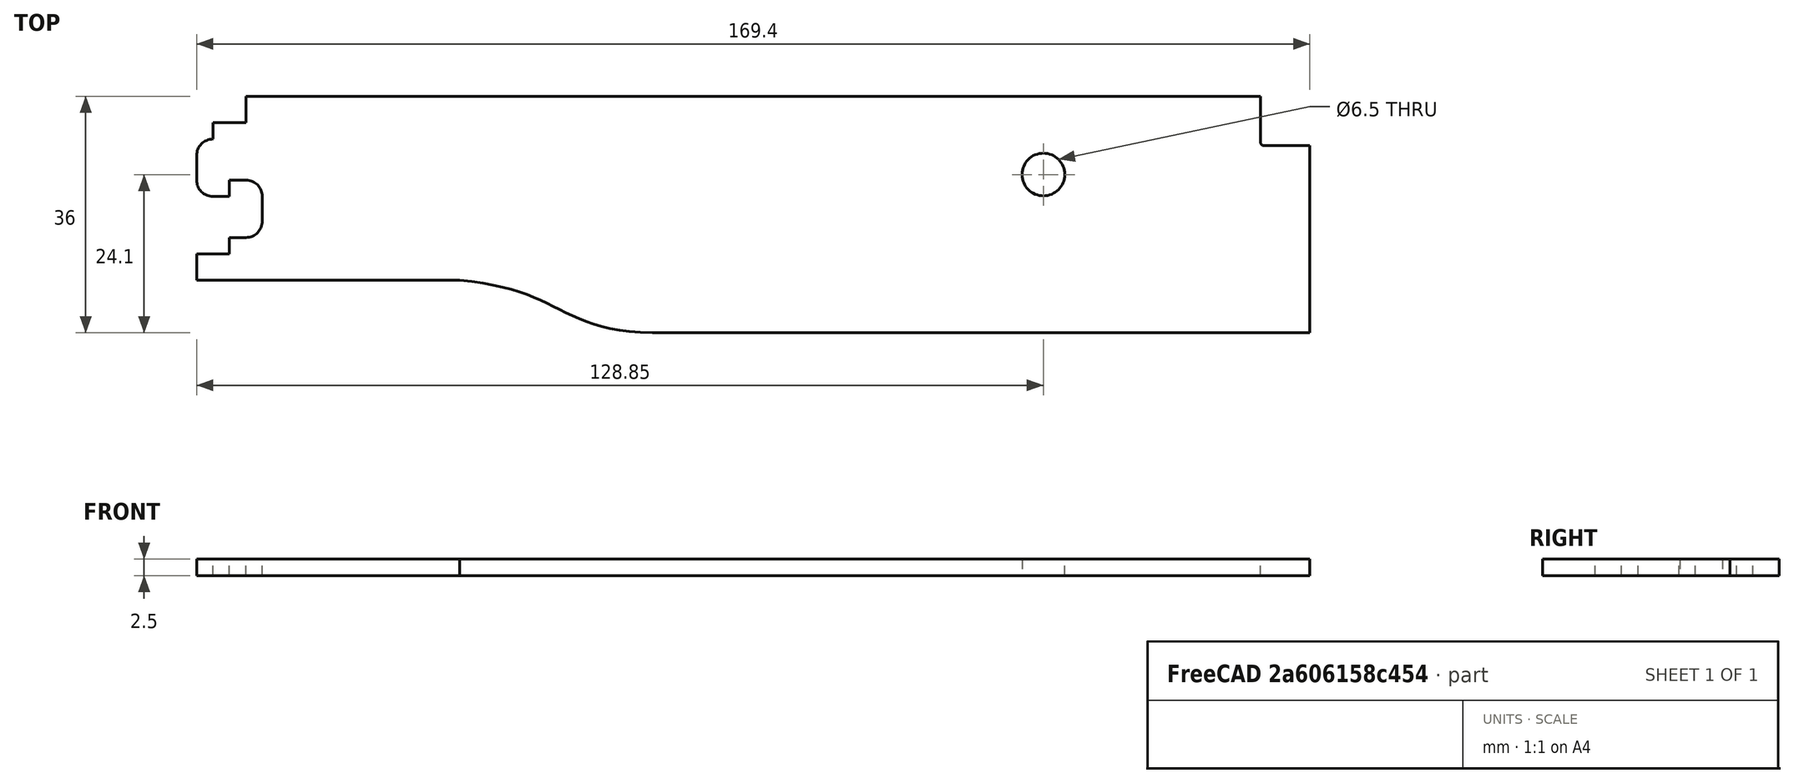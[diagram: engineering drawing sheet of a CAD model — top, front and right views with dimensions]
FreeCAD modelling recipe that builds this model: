
FCSTD DOCUMENT  (FreeCAD 0.19R0.19.2)
Label: v0_11
License: All rights reserved
LicenseURL: http://en.wikipedia.org/wiki/All_rights_reserved
objects: Sketcher::SketchObject×2, Part::Extrusion×1
note: 3 computed .brp shape members not serialized (recipe doc carries the construction recipe); baked Part::Feature solids carry a one-line shape summary decoded from their .brp

FEATURE [Sketcher::SketchObject] Sketch
  FullyConstrained = true
  sketch-geometry (33):
    g0: LineSegment StartX=0 StartY=0 StartZ=0 EndX=154.4 EndY=0 EndZ=0
    g1: LineSegment StartX=154.4 StartY=0 StartZ=0 EndX=154.4 EndY=-7 EndZ=0
    g2: LineSegment StartX=154.9 StartY=-7.5 StartZ=0 EndX=161.9 EndY=-7.5 EndZ=0
    g3: ArcOfCircle CenterX=154.9 CenterY=-7 CenterZ=0 NormalX=0 NormalY=0 NormalZ=1 AngleXU=0 Radius=0.5 StartAngle=3.14159 EndAngle=4.71239
    g4: Circle CenterX=121.35 CenterY=-11.9 CenterZ=0 NormalX=0 NormalY=0 NormalZ=1 AngleXU=0 Radius=3.25
    g5: LineSegment StartX=0 StartY=0 StartZ=0 EndX=0 EndY=-4 EndZ=0
    g6: LineSegment StartX=-5 StartY=-4 StartZ=0 EndX=0 EndY=-4 EndZ=0
    g7: LineSegment StartX=-5 StartY=-4 StartZ=0 EndX=-5 EndY=-6.5 EndZ=0
    g8: LineSegment StartX=-7.5 StartY=-9 StartZ=0 EndX=-7.5 EndY=-12.75 EndZ=0
    g9: ArcOfCircle CenterX=-5 CenterY=-9 CenterZ=0 NormalX=0 NormalY=0 NormalZ=1 AngleXU=0 Radius=2.5 StartAngle=1.5708 EndAngle=3.14159
    g10: LineSegment StartX=-5 StartY=-15.25 StartZ=0 EndX=-2.5 EndY=-15.25 EndZ=0
    g11: ArcOfCircle CenterX=-5 CenterY=-12.75 CenterZ=0 NormalX=0 NormalY=0 NormalZ=1 AngleXU=0 Radius=2.5 StartAngle=3.14159 EndAngle=4.71239
    g12: LineSegment StartX=-2.5 StartY=-15.25 StartZ=0 EndX=-2.5 EndY=-12.75 EndZ=0
    g13: LineSegment StartX=-2.5 StartY=-12.75 StartZ=0 EndX=1.488e-13 EndY=-12.75 EndZ=0
    g14: ArcOfCircle CenterX=1.486e-13 CenterY=-15.25 CenterZ=0 NormalX=0 NormalY=0 NormalZ=1 AngleXU=0 Radius=2.5 StartAngle=8e-16 EndAngle=1.5708
    g15: LineSegment StartX=2.5 StartY=-15.25 StartZ=0 EndX=2.5 EndY=-19 EndZ=0
    g16: ArcOfCircle CenterX=1.483e-13 CenterY=-19 CenterZ=0 NormalX=0 NormalY=0 NormalZ=1 AngleXU=0 Radius=2.5 StartAngle=4.71239 EndAngle=6.28319
    g17: LineSegment StartX=-2.5 StartY=-21.5 StartZ=0 EndX=1.479e-13 EndY=-21.5 EndZ=0
    g18: LineSegment StartX=-2.5 StartY=-21.5 StartZ=0 EndX=-2.5 EndY=-24 EndZ=0
    g19: LineSegment StartX=-7.5 StartY=-24 StartZ=0 EndX=-2.5 EndY=-24 EndZ=0
    g20: LineSegment StartX=-7.5 StartY=-24 StartZ=0 EndX=-7.5 EndY=-28 EndZ=0
    g21: LineSegment StartX=161.9 StartY=-7.5 StartZ=0 EndX=161.9 EndY=-36 EndZ=0
    g22: LineSegment StartX=61.85 StartY=-36 StartZ=0 EndX=161.9 EndY=-36 EndZ=0
    g23-g27: Circle x5 (B-spline internal-alignment scaffolding for g28; pole/knot coordinates omitted)
    g28: BSplineCurve PolesCount=5 KnotsCount=3 Degree=3 IsPeriodic=0
    g29: GeomPoint X=61.85 Y=-36 Z=0
    g30: GeomPoint X=47.2264 Y=-32.2128 Z=0
    g31: GeomPoint X=32.5209 Y=-28 Z=0
    g32: LineSegment StartX=32.5209 StartY=-28 StartZ=0 EndX=-7.5 EndY=-28 EndZ=0
  constraints (75):
    c: PointOnObject(g0,g-2)
    c: Horizontal(g0)
    c: Distance(g0) = 154.4
    c: DistanceY(g-1,g0) = 0
    c: Vertical(g1)
    c: Distance(g1) = 7
    c: Coincident(g1,g0)
    c: Horizontal(g2)
    c: Distance(g2) = 7
    c: Coincident(g3,g1)
    c: Tangent(g2,g3)
    c: Tangent(g2,g3,g2) = -1.5708
    c: Block(g3)
    c: Block(g4)
    c: Vertical(g5)
    c: Distance(g5) = 4
    c: Coincident(g5,g0)
    c: Horizontal(g6)
    c: Distance(g6) = 5
    c: Coincident(g6,g5)
    c: Vertical(g7)
    c: Distance(g7) = 2.5
    c: Coincident(g7,g6)
    c: Vertical(g8)
    c: Distance(g8) = 3.75
    c: Coincident(g9,g7)
    c: Block(g9)
    c: Coincident(g8,g9)
    c: Horizontal(g10)
    c: Distance(g10) = 2.5
    c: Coincident(g11,g8)
    c: Block(g11)
    c: Block(g10)
    c: Vertical(g12)
    c: Distance(g12) = 2.5
    c: Coincident(g12,g10)
    c: Horizontal(g13)
    c: Distance(g13) = 2.5
    c: Coincident(g13,g12)
    c: Coincident(g14,g13)
    c: Vertical(g15)
    c: Distance(g15) = 3.75
    c: Block(g14)
    c: Coincident(g15,g14)
    c: Coincident(g16,g15)
    c: Block(g16)
    c: Horizontal(g17)
    c: Distance(g17) = 2.5
    c: Coincident(g17,g16)
    c: Vertical(g18)
    c: Distance(g18) = 2.5
    c: Coincident(g18,g17)
    c: Horizontal(g19)
    c: Distance(g19) = 5
    c: Coincident(g19,g18)
    c: Vertical(g20)
    c: Distance(g20) = 4
    c: Coincident(g20,g19)
    c: Vertical(g21)
    c: Distance(g21) = 28.5
    c: Coincident(g21,g2)
    c: Horizontal(g22)
    c: Distance(g22) = 100.05
    c: Coincident(g22,g21)
    c: Coincident(g28,g22)
    c: Weight(g23) = 1
    c: Equal(g23, g24-g27) x4
    c: InternalAlignment(g23-g27 -> g28) x5
    c: InternalAlignment(g29,g28)
    c: InternalAlignment(g30,g28)
    c: InternalAlignment(g31,g28)
    c: Horizontal(g32)
    c: Coincident(g32,g20)
    c: Coincident(g32,g28)
    c: Block(g28)
FEATURE [Part::Extrusion] Extrude
  Base = -> Sketch
  Dir = (0,0,1)
  DirMode = 2
  FaceMakerClass = Part::FaceMakerBullseye
  LengthFwd = 2.5
  LengthRev = 0
  Solid = true
  Symmetric = false
FEATURE [Sketcher::SketchObject] Sketch001
  FullyConstrained = true
  sketch-geometry (60):
    g0: LineSegment StartX=0 StartY=0 StartZ=0 EndX=154.4 EndY=0 EndZ=0
    g1: LineSegment StartX=154.9 StartY=-7.5 StartZ=0 EndX=161.9 EndY=-7.5 EndZ=0
    g2: ArcOfCircle CenterX=154.9 CenterY=-7 CenterZ=0 NormalX=0 NormalY=0 NormalZ=1 AngleXU=0 Radius=0.5 StartAngle=3.14159 EndAngle=4.71239
    g3: Circle CenterX=121.35 CenterY=-11.9 CenterZ=0 NormalX=0 NormalY=0 NormalZ=1 AngleXU=0 Radius=3.25
    g4: LineSegment StartX=0 StartY=0 StartZ=0 EndX=0 EndY=-4 EndZ=0
    g5: LineSegment StartX=-5 StartY=-4 StartZ=0 EndX=0 EndY=-4 EndZ=0
    g6: LineSegment StartX=-5 StartY=-4 StartZ=0 EndX=-5 EndY=-6.5 EndZ=0
    g7: LineSegment StartX=-7.50066 StartY=-9 StartZ=0 EndX=-7.50066 EndY=-12.75 EndZ=0
    g8: ArcOfCircle CenterX=-5.00066 CenterY=-9 CenterZ=0 NormalX=0 NormalY=0 NormalZ=1 AngleXU=0 Radius=2.5 StartAngle=1.57053 EndAngle=3.14159
    g9: LineSegment StartX=-5 StartY=-15.25 StartZ=0 EndX=-2.5 EndY=-15.25 EndZ=0
    g10: ArcOfCircle CenterX=-5 CenterY=-12.75 CenterZ=0 NormalX=0 NormalY=0 NormalZ=1 AngleXU=0 Radius=2.50066 StartAngle=3.14159 EndAngle=4.71239
    g11: LineSegment StartX=-2.5 StartY=-15.25 StartZ=0 EndX=-2.5 EndY=-12.75 EndZ=0
    g12: LineSegment StartX=-2.5 StartY=-12.75 StartZ=0 EndX=1.488e-13 EndY=-12.75 EndZ=0
    g13: ArcOfCircle CenterX=1.486e-13 CenterY=-15.25 CenterZ=0 NormalX=0 NormalY=0 NormalZ=1 AngleXU=0 Radius=2.5 StartAngle=8e-16 EndAngle=1.5708
    g14: LineSegment StartX=2.5 StartY=-15.25 StartZ=0 EndX=2.5 EndY=-19 EndZ=0
    g15: ArcOfCircle CenterX=1.483e-13 CenterY=-19 CenterZ=0 NormalX=0 NormalY=0 NormalZ=1 AngleXU=0 Radius=2.5 StartAngle=4.71239 EndAngle=6.28319
    g16: LineSegment StartX=-2.5 StartY=-21.5 StartZ=0 EndX=1.812e-13 EndY=-21.5 EndZ=0
    g17: LineSegment StartX=-2.5 StartY=-21.5 StartZ=0 EndX=-2.5 EndY=-24 EndZ=0
    g18: LineSegment StartX=-7.5 StartY=-24 StartZ=0 EndX=-2.5 EndY=-24 EndZ=0
    g19: LineSegment StartX=-7.5 StartY=-24 StartZ=0 EndX=-7.5 EndY=-28 EndZ=0
    g20: LineSegment StartX=161.9 StartY=-7.5 StartZ=0 EndX=161.9 EndY=-36 EndZ=0
    g21: LineSegment StartX=61.85 StartY=-36 StartZ=0 EndX=161.9 EndY=-36 EndZ=0
    g22-g26: Circle x5 (B-spline internal-alignment scaffolding for g27; pole/knot coordinates omitted)
    g27: BSplineCurve PolesCount=5 KnotsCount=3 Degree=3 IsPeriodic=0
    g28: GeomPoint X=61.85 Y=-36 Z=0
    g29: GeomPoint X=47.2264 Y=-32.2128 Z=0
    g30: GeomPoint X=32.5209 Y=-28 Z=0
    g31: LineSegment StartX=154.4 StartY=0 StartZ=0 EndX=154.4 EndY=-3 EndZ=0
    g32: ArcOfCircle CenterX=154.9 CenterY=-7 CenterZ=0 NormalX=0 NormalY=0 NormalZ=1 AngleXU=0 Radius=3.5 StartAngle=3.14159 EndAngle=4.71239
    g33: LineSegment StartX=161.9 StartY=-7.5 StartZ=0 EndX=161.9 EndY=-10.5 EndZ=0
    g34: Circle CenterX=121.35 CenterY=-11.9 CenterZ=0 NormalX=0 NormalY=0 NormalZ=1 AngleXU=0 Radius=6.25
    g35: LineSegment StartX=154.9 StartY=-10.5 StartZ=0 EndX=158.4 EndY=-10.5 EndZ=0
    g36: ArcOfCircle CenterX=158.4 CenterY=-11 CenterZ=0 NormalX=0 NormalY=0 NormalZ=1 AngleXU=0 Radius=0.5 StartAngle=0 EndAngle=1.5708
    g37: LineSegment StartX=161.9 StartY=-36 StartZ=0 EndX=158.9 EndY=-36 EndZ=0
    g38: ArcOfCircle CenterX=158.4 CenterY=-32.5 CenterZ=0 NormalX=0 NormalY=0 NormalZ=1 AngleXU=0 Radius=0.5 StartAngle=4.71239 EndAngle=6.28319
    g39: LineSegment StartX=158.9 StartY=-11 StartZ=0 EndX=158.9 EndY=-32.5 EndZ=0
    g40: LineSegment StartX=61.85 StartY=-33 StartZ=0 EndX=158.4 EndY=-33 EndZ=0
    g41: LineSegment StartX=151.4 StartY=-7 StartZ=0 EndX=151.4 EndY=-3.5 EndZ=0
    g42: ArcOfCircle CenterX=150.9 CenterY=-3.5 CenterZ=0 NormalX=0 NormalY=0 NormalZ=1 AngleXU=0 Radius=0.5 StartAngle=-5.0484e-12 EndAngle=1.5708
    g43: LineSegment StartX=0 StartY=0 StartZ=0 EndX=5 EndY=0 EndZ=0
    g44: ArcOfCircle CenterX=8 CenterY=-6 CenterZ=0 NormalX=0 NormalY=0 NormalZ=1 AngleXU=0 Radius=3 StartAngle=1.5708 EndAngle=3.14159
    g45: LineSegment StartX=8 StartY=-3 StartZ=0 EndX=150.9 EndY=-3 EndZ=0
    g46: LineSegment StartX=154.4 StartY=-3 StartZ=0 EndX=154.4 EndY=-7 EndZ=0
    g47: LineSegment StartX=5 StartY=-6 StartZ=0 EndX=5 EndY=-22 EndZ=0
    g48: LineSegment StartX=-7.5 StartY=-28 StartZ=0 EndX=32.5209 EndY=-28 EndZ=0
    g49: ArcOfCircle CenterX=8 CenterY=-22 CenterZ=0 NormalX=0 NormalY=0 NormalZ=1 AngleXU=0 Radius=3 StartAngle=3.14159 EndAngle=4.71239
    g50: LineSegment StartX=8 StartY=-25 StartZ=0 EndX=32.52 EndY=-25 EndZ=0
    g51-g55: Circle x5 (B-spline internal-alignment scaffolding for g56; pole/knot coordinates omitted)
    g56: BSplineCurve PolesCount=5 KnotsCount=3 Degree=3 IsPeriodic=0
    g57: GeomPoint X=32.52 Y=-25 Z=0
    g58: GeomPoint X=47.2188 Y=-29.105 Z=0
    g59: GeomPoint X=61.85 Y=-33 Z=0
  constraints (127):
    c: PointOnObject(g0,g-2)
    c: Horizontal(g0)
    c: Distance(g0) = 154.4
    c: DistanceY(g-1,g0) = 0
    c: Horizontal(g1)
    c: Distance(g1) = 7
    c: Tangent(g1,g2)
    c: Tangent(g1,g2,g1) = -1.5708
    c: Block(g2)
    c: Block(g3)
    c: Vertical(g4)
    c: Distance(g4) = 4
    c: Coincident(g4,g0)
    c: Horizontal(g5)
    c: Distance(g5) = 5
    c: Coincident(g5,g4)
    c: Vertical(g6)
    c: Distance(g6) = 2.5
    c: Coincident(g6,g5)
    c: Vertical(g7)
    c: Distance(g7) = 3.75
    c: Coincident(g8,g6)
    c: Block(g8)
    c: Coincident(g7,g8)
    c: Horizontal(g9)
    c: Distance(g9) = 2.5
    c: Coincident(g10,g7)
    c: Block(g10)
    c: Block(g9)
    c: Vertical(g11)
    c: Distance(g11) = 2.5
    c: Coincident(g11,g9)
    c: Horizontal(g12)
    c: Distance(g12) = 2.5
    c: Coincident(g12,g11)
    c: Coincident(g13,g12)
    c: Vertical(g14)
    c: Distance(g14) = 3.75
    c: Block(g13)
    c: Coincident(g14,g13)
    c: Coincident(g15,g14)
    c: Block(g15)
    c: Horizontal(g16)
    c: Distance(g16) = 2.5
    c: Coincident(g16,g15)
    c: Vertical(g17)
    c: Distance(g17) = 2.5
    c: Coincident(g17,g16)
    c: Horizontal(g18)
    c: Distance(g18) = 5
    c: Coincident(g18,g17)
    c: Vertical(g19)
    c: Distance(g19) = 4
    c: Coincident(g19,g18)
    c: Vertical(g20)
    c: Distance(g20) = 28.5
    c: Coincident(g20,g1)
    c: Horizontal(g21)
    c: Distance(g21) = 100.05
    c: Coincident(g21,g20)
    c: Coincident(g27,g21)
    c: Weight(g22) = 1
    c: Equal(g22, g23-g26) x4
    c: InternalAlignment(g22-g26 -> g27) x5
    c: InternalAlignment(g28,g27)
    c: InternalAlignment(g29,g27)
    c: InternalAlignment(g30,g27)
    c: Block(g27)
    c: Vertical(g31)
    c: Distance(g31) = 3
    c: Coincident(g31,g0)
    c: Coincident(g32,g2)
    c: Vertical(g33)
    c: Distance(g33) = 3
    c: Coincident(g33,g1)
    c: Block(g32)
    c: Coincident(g34,g3)
    c: Block(g34)
    c: Horizontal(g35)
    c: Distance(g35) = 3.5
    c: Coincident(g35,g32)
    c: Coincident(g36,g35)
    c: Block(g36)
    c: Horizontal(g37)
    c: Distance(g37) = 3
    c: Coincident(g37,g20)
    c: Block(g38)
    c: Vertical(g39)
    c: Coincident(g39,g38)
    c: Coincident(g39,g36)
    c: Horizontal(g40)
    c: Coincident(g40,g38)
    c: Distance(g40) = 96.55
    c: Vertical(g41)
    c: Distance(g41) = 3.5
    c: Coincident(g41,g32)
    c: Coincident(g42,g41)
    c: Block(g42)
    c: Horizontal(g43)
    c: Distance(g43) = 5
    c: Coincident(g43,g0)
    c: Block(g44)
    c: Horizontal(g45)
    c: Coincident(g45,g44)
    c: Coincident(g45,g42)
    c: Vertical(g46)
    c: Coincident(g46,g31)
    c: Coincident(g46,g2)
    c: Vertical(g47)
    c: Coincident(g47,g44)
    c: Horizontal(g48)
    c: Coincident(g48,g19)
    c: Coincident(g48,g27)
    c: Coincident(g49,g47)
    c: Block(g49)
    c: Horizontal(g50)
    c: Coincident(g50,g49)
    c: Distance(g50) = 24.52
    c: Coincident(g56,g50)
    c: Weight(g51) = 1
    c: Equal(g51, g52-g55) x4
    c: Coincident(g56,g40)
    c: InternalAlignment(g51-g55 -> g56) x5
    c: InternalAlignment(g57,g56)
    c: InternalAlignment(g58,g56)
    c: InternalAlignment(g59,g56)
    c: Block(g56)
